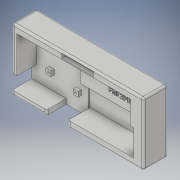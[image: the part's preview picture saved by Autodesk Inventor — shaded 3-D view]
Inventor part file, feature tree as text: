
AUTODESK INVENTOR PART (.ipt)
format: ipt  version: 2017 (Build 210142000, 142)  size: 523,264 bytes
history: native  units: in
note: dims shown in document units (in); Inventor stores cm internally (conversion verified against a paired STEP export)
features: extrude x10, sketch x10, fillet x2
ambient origin geometry x8: Origin, YZ Plane, XZ Plane, XY Plane, X Axis, Y Axis, Z Axis, Center Point
bodies: Solid1 (feature_tree)
feature tree (22):
  extrude  "Extrusion1"  Depth=2.5197in
  extrude  "Extrusion2"  Depth=2.0472in
  extrude  "Extrusion3"  Depth=0.7874in TaperAngle=0.0deg
  extrude  "Extrusion4"  Depth=1.0433in
  extrude  "Extrusion5"  Depth=0.5118in
  extrude  "Extrusion6"  Depth=2.4803in
  extrude  "Extrusion7"  Depth=1.9685in
  extrude  "Extrusion8"  Depth=0.1181in
  extrude  "Extrusion9"  Depth=0.6575in
  fillet  "Fillet1"  Radius=0.563in
  fillet  "Fillet3"  Radius=0.4921in
  extrude  "Extrusion10"  Depth=0.1969in
  sketch  "Sketch1"  dims[d0=5.2362in d1=2.5197in]
  sketch  "Sketch2"  dims[d2=0.9843in d3=0.0in d10=2.0472in]
  sketch  "Sketch3"  dims[d11=2.0472in d12=0.7874in d13=0.0in]
  sketch  "Sketch4"  dims[d15=2.5984in d16=1.0433in]
  sketch  "Sketch5"  dims[d17=0.8661in d18=0.0in d19=0.5118in]
  sketch  "Sketch6"  dims[d20=0.9843in d21=0.0in d22=2.4803in]
  sketch  "Sketch7"  dims[d23=0.4724in d24=0.0in d25=1.9685in]
  sketch  "Sketch8"  dims[d26=1.9685in d27=0.1181in]
  sketch  "Sketch9"  dims[d28=0.1732in d29=0.6575in d30=0.563in d31=0.4921in]
  sketch  "Sketch10"  dims[d32=0.3189in d33=0.1969in d34=0.1969in d35=0.1969in d36=0.1969in d37=0.1969in d38=0.1969in d39=0.1378in d40=0.0in d41=0.8661in d42=0.5906in d43=0.7874in d44=0.0in d49=1.2598in d50=0.1575in d51=0.0in d52=0.0591in d53=0.0in d54=0.0787in d56=0.0787in d57=0.0787in d58=0.0787in d59=0.0787in d60=0.0394in d61=0.0in]
